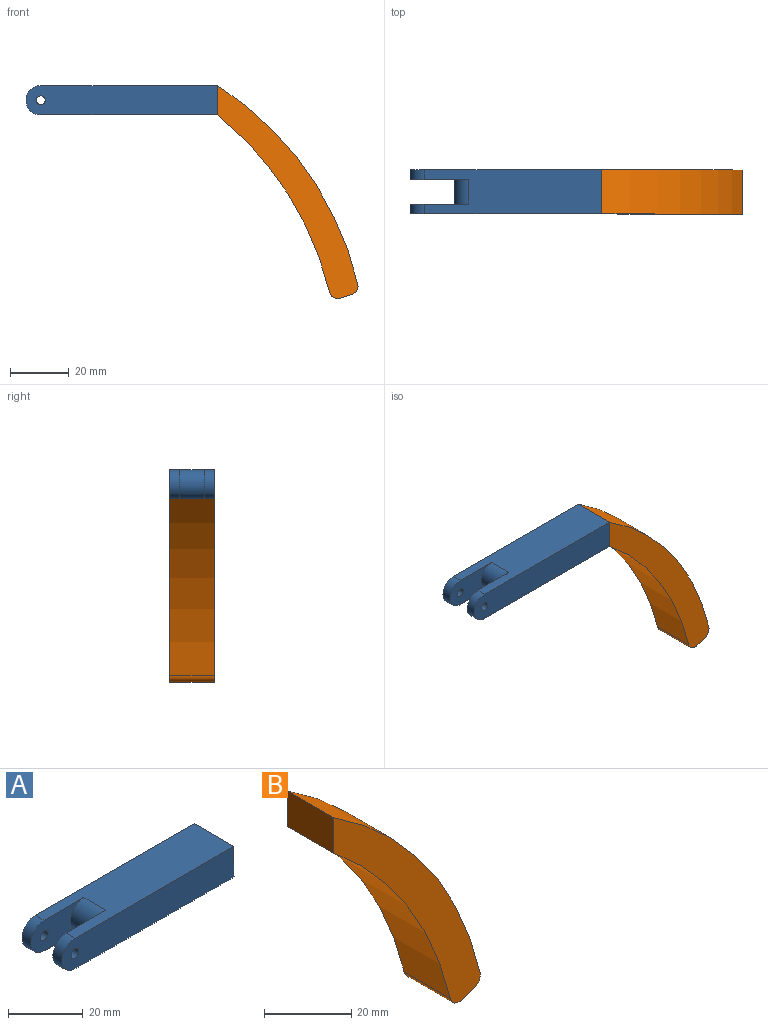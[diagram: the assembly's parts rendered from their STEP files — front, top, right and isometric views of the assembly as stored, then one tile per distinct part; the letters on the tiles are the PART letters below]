
ASSEMBLY  parts=2 mates=1
PART A: 12 faces, bbox 65x15x10 mm
  f0: plane 65x10mm, normal (0,1,0), area 632.2mm2, adj f2,f3,f7,f8,f9
  f1: plane 65x10mm, normal (0,-1,0), area 632.2mm2, adj f2,f3,f6,f8,f11
  f2: plane 60x15mm, normal (0,0,1), area 775.5mm2, adj f0,f1,f4,f5,f8,f9,f10,f11
  f3: plane 60x15mm, normal (0,0,-1), area 775.5mm2, adj f0,f1,f4,f5,f8,f9,f10,f11
  f4: plane 20x10mm, normal (0,-1,0), area 142.9mm2, adj f2,f3,f7,f9,f10
  f5: plane 20x10mm, normal (0,1,0), area 142.9mm2, adj f2,f3,f6,f10,f11
  f6: cylinder r=1.5mm len=3.35mm, axis (0,1,0), area 31.6mm2, adj f1,f5
  f7: cylinder r=1.5mm len=3.35mm, axis (0,1,0), area 31.6mm2, adj f0,f4
  f8: plane 15x10mm, normal (1,0,0), area 150mm2, adj f0,f1,f2,f3
  f9: cylinder r=5mm len=10mm, axis (0,1,0), area 52.6mm2, adj f0,f2,f3,f4
  f10: cylinder r=5mm len=10mm, axis (0,-1,0), area 130.4mm2, adj f2,f3,f4,f5
  f11: cylinder r=5mm len=10mm, axis (0,1,0), area 52.6mm2, adj f1,f2,f3,f5
PART B: 8 faces, bbox 47.6x15x72.2 mm
  f0: plane 72.25x47.62mm, normal (0,-1,0), area 766.3mm2, adj f1,f2,f3,f4,f6,f7
  f1: plane 15x3.8mm, normal (0.3,0,-0.95), area 59.8mm2, adj f0,f5,f6,f7
  f2: plane 15x10mm, normal (-1,0,0), area 150mm2, adj f0,f3,f4,f5
  f3: cylinder r=110mm len=67.35mm, axis (0,1,0), area 1267.4mm2, adj f0,f2,f5,f6
  f4: cylinder r=110mm len=59.95mm, axis (0,1,0), area 1083.2mm2, adj f0,f2,f5,f7
  f5: plane 72.25x47.62mm, normal (0,1,0), area 766.3mm2, adj f1,f2,f3,f4,f6,f7
  f6: cylinder r=3mm len=15mm, axis (0,1,0), area 67.1mm2, adj f0,f1,f3,f5
  f7: cylinder r=3mm len=15mm, axis (0,1,0), area 74mm2, adj f0,f1,f4,f5
PLACE A t=(12.48,-10.7,10.91)mm
PLACE B t=(12.48,4.3,10.91)mm
MATE parallel B.f2 <-> A.f8  axis (-1,0,0) through (-33.76,-18.2,29.99)mm
